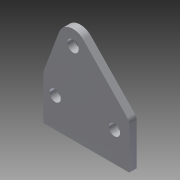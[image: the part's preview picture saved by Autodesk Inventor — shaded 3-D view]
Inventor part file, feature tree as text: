
AUTODESK INVENTOR PART (.ipt)
format: ipt  version: 2014 (Build 180170000, 170)  size: 101,376 bytes
history: native  units: in
note: dims shown in document units (in); Inventor stores cm internally (conversion verified against a paired STEP export)
features: extrude x1, fillet x1, sketch x1
ambient origin geometry x8: Origin, YZ Plane, XZ Plane, XY Plane, X Axis, Y Axis, Z Axis, Center Point
bodies: Solid1 (feature_tree)
feature tree (3):
  extrude  "Extrusion1"  Depth=0.125in TaperAngle=0.0deg
  fillet  "Fillet1"  Radius=0.5in
  sketch  "Sketch1"  dims[d1=0.19in d3=0.125in d4=0.0in d5=0.5in d6=0.25in d7=0.2in d9=0.25in d10=1.0in d14=0.5in d15=0.625in d16=0.194in d17=0.25in d18=0.125in]
